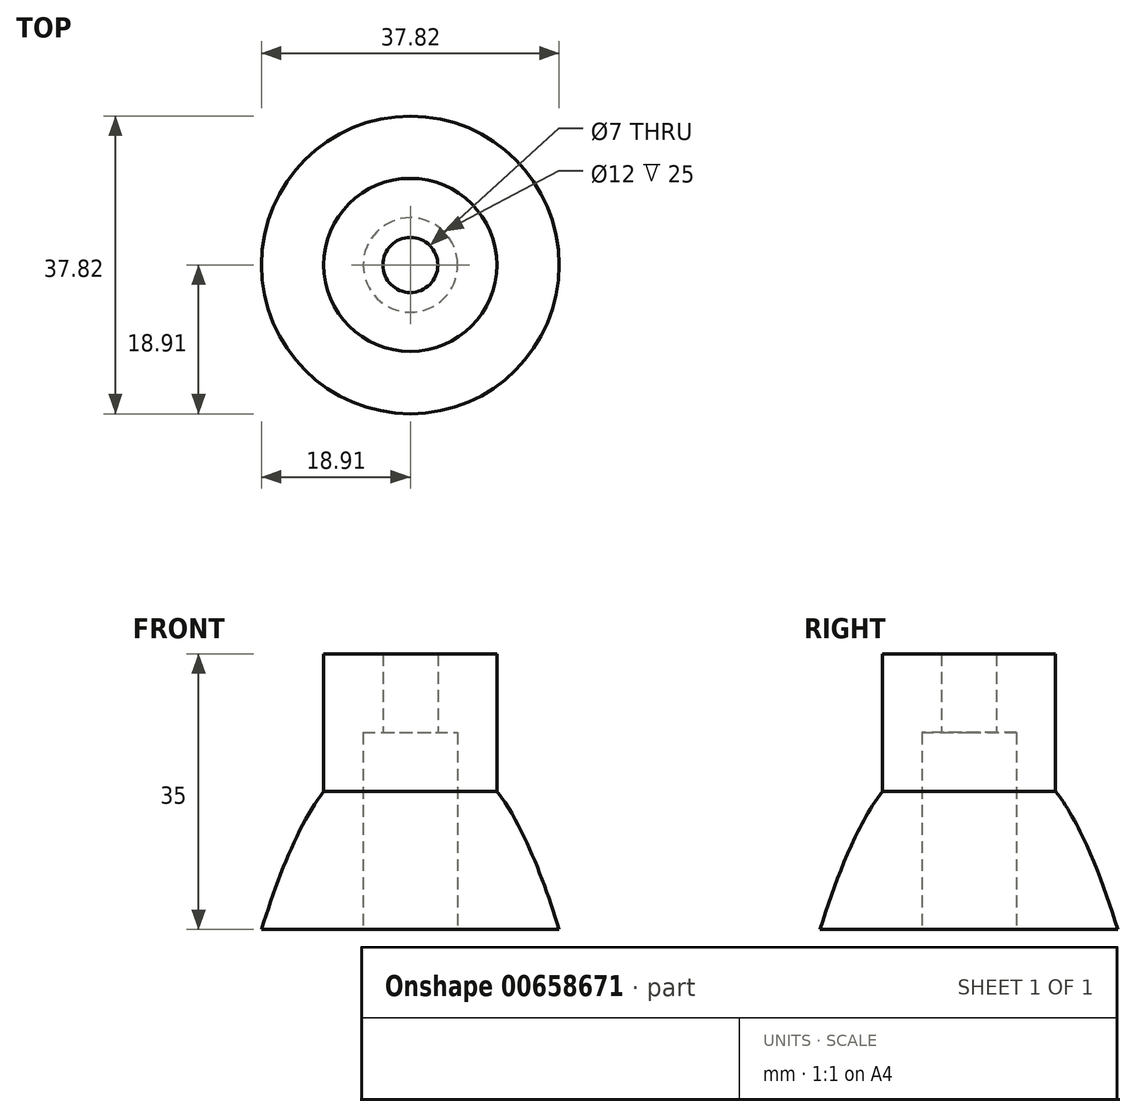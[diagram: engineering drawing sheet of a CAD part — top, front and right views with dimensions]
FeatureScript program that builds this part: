
annotation { "Feature Type Name" : "Feature", "Feature Type Description" : "" }
export const myFeature = defineFeature(function(context is Context, id is Id, definition is map)
    precondition{}
    {
        {
            var Q0;
            Q0=qCreatedBy(makeId("Front.planeOp"),FACE);
            var sketch = newSketch(context, id + "F0", { "sketchPlane" : qUnion([Q0])});
            skLineSegment(sketch, "E0", {"start": v(3.5, 20) * mm, "end": v(3.5, 10) * mm});
            skLineSegment(sketch, "E1", {"start": v(3.5, 10) * mm, "end": v(6, 10) * mm});
            skLineSegment(sketch, "E2", {"start": v(6, 10) * mm, "end": v(6, -15) * mm});
            skLineSegment(sketch, "E3", {"start": v(6, -15) * mm, "end": v(11, -15) * mm});
            skLineSegment(sketch, "E4", {"start": v(11, -15) * mm, "end": v(11, 20) * mm});
            skLineSegment(sketch, "E5", {"start": v(11, 20) * mm, "end": v(3.5, 20) * mm});
            skFitSpline(sketch, "E6", {"points": [v(11, 2.5) * mm, v(22.15, -26.8) * mm, v(24.95, -43.24) * mm], "startDerivative": vector(25.33, -31.45) * mm, "endDerivative": vector(2.2, -35.08) * mm});
            skLineSegment(sketch, "E7", {"start": v(11, -15) * mm, "end": v(18.9, -15) * mm});
            skLineSegment(sketch, "E8", {"start": v(0, 0) * mm, "end": v(0, 7.37) * mm});
            skSolve(sketch);
        }
        {
            var Q0;
            {var subQ2=sQuery(id+"F0.wireOp",EDGE,"E6");Q0=makeQuery(id+"F0.imprint","IMPRINT",FACE,{"disambiguationData":[TD([[makeQuery(id+"F0.imprint","IMPRINT",EDGE,{"derivedFrom":subQ2}),-1.0]])]});}
            var Q1;
            Q1=makeQuery(id+"F0.imprint","IMPRINT",FACE,{"disambiguationData":[TD([[makeQuery(id+"F0.imprint","IMPRINT",EDGE,{"derivedFrom":sQuery(id+"F0.wireOp",EDGE,"E0")}),1.0]])]});
            var Q2;
            Q2=sQuery(id+"F0.wireOp",EDGE,"E8");
            revolve(context, id + "F1", {"entities" : qUnion([Q0, Q1]), "axis" : qUnion([Q2]), "revolveType" : RevolveType.FULL});
        }
    });
